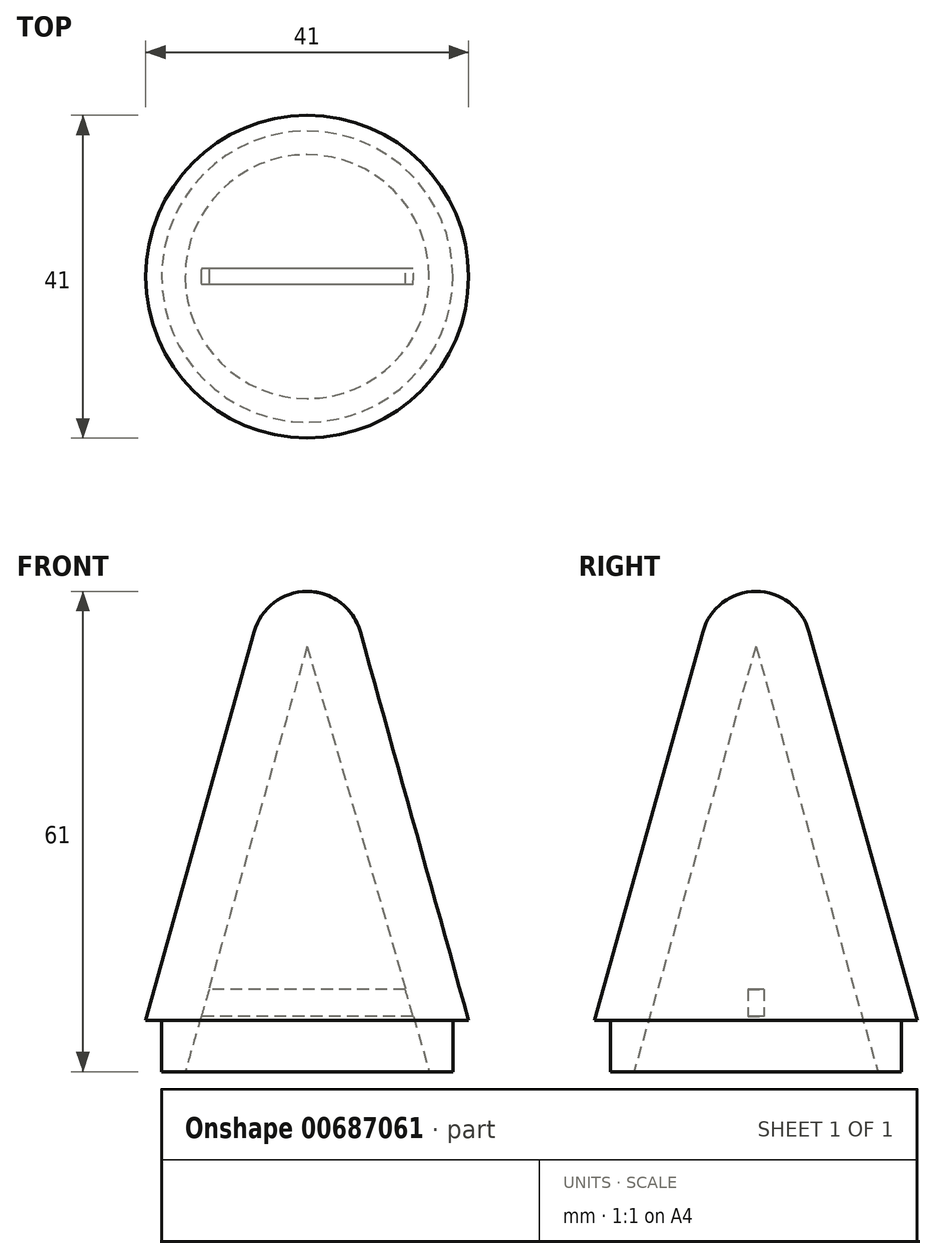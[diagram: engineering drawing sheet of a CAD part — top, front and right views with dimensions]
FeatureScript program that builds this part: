
annotation { "Feature Type Name" : "Feature", "Feature Type Description" : "" }
export const myFeature = defineFeature(function(context is Context, id is Id, definition is map)
    precondition{}
    {
        {
            var Q0;
            Q0=qCreatedBy(makeId("Front.planeOp"),FACE);
            var sketch = newSketch(context, id + "F0", { "sketchPlane" : qUnion([Q0])});
            skArc(sketch, "E0", {"start": v(6.74, 52.38) * mm, "mid": v(4.23, 56.07) * mm, "end": v(0, 57.5) * mm});
            skLineSegment(sketch, "E1", {"start": v(0, 50.5) * mm, "end": v(15.5, -3.5) * mm});
            skLineSegment(sketch, "E2", {"start": v(6.74, 52.38) * mm, "end": v(20.5, 3) * mm});
            skLineSegment(sketch, "E3", {"start": v(20.5, 3) * mm, "end": v(18.5, 3) * mm});
            skLineSegment(sketch, "E4", {"start": v(18.5, 3) * mm, "end": v(18.5, -3.5) * mm});
            skLineSegment(sketch, "E5", {"start": v(18.5, -3.5) * mm, "end": v(15.5, -3.5) * mm});
            skLineSegment(sketch, "E6", {"start": v(0, 57.5) * mm, "end": v(0, 0) * mm});
            skLineSegment(sketch, "E7", {"start": v(0, 50.92) * mm, "end": v(-0.12, 50.92) * mm});
            skLineSegment(sketch, "E8", {"start": v(15.5, -3.5) * mm, "end": v(15.5, -3.5) * mm});
            skLineSegment(sketch, "E9", {"start": v(15.5, -3.5) * mm, "end": v(0, -3.5) * mm});
            skSolve(sketch);
        }
        {
            var Q0;
            Q0 = qSketchRegion(id + "F0", true);
            var Q1;
            Q1=sQuery(id+"F0.wireOp",EDGE,"E6");
            revolve(context, id + "F1", {"surfaceOperationType" : NewSurfaceOperationType.NEW, "entities" : qUnion([Q0]), "axis" : qUnion([Q1]), "revolveType" : RevolveType.FULL});
        }
        {
            var Q0;
            Q0=qCreatedBy(makeId("Right.planeOp"),FACE);
            var sketch = newSketch(context, id + "F2", { "sketchPlane" : qUnion([Q0])});
            skLineSegment(sketch, "E10.bottom", {"start": v(-1.04, 3.54) * mm, "end": v(1.04, 3.54) * mm});
            skLineSegment(sketch, "E10.top", {"start": v(-1.04, 6.97) * mm, "end": v(1.04, 6.97) * mm});
            skLineSegment(sketch, "E10.left", {"start": v(-1.04, 3.54) * mm, "end": v(-1.04, 6.97) * mm});
            skLineSegment(sketch, "E10.right", {"start": v(1.04, 3.54) * mm, "end": v(1.04, 6.97) * mm});
            skPoint(sketch, "E10.middle", {"position": v(0, 5.26) * mm});
            skSolve(sketch);
        }
        {
            var Q0;
            Q0 = qSketchRegion(id + "F2", true);
            var Q1;
            Q1=makeQuery(id+"F1.opRevolve","SWEPT_BODY",BODY,{"disambiguationData":[OSD([sQuery(id+"F0.wireOp",EDGE,"E0"),sQuery(id+"F0.wireOp",EDGE,"E1"),sQuery(id+"F0.wireOp",EDGE,"E2"),sQuery(id+"F0.wireOp",EDGE,"E3"),sQuery(id+"F0.wireOp",EDGE,"E4"),sQuery(id+"F0.wireOp",EDGE,"E5"),sQuery(id+"F0.wireOp",EDGE,"E6")])]});
            var Q2;
            Q2=makeQuery(id+"F1.opRevolve","SWEPT_BODY",BODY,{"disambiguationData":[OSD([sQuery(id+"F0.wireOp",EDGE,"E0"),sQuery(id+"F0.wireOp",EDGE,"E1"),sQuery(id+"F0.wireOp",EDGE,"E2"),sQuery(id+"F0.wireOp",EDGE,"E3"),sQuery(id+"F0.wireOp",EDGE,"E4"),sQuery(id+"F0.wireOp",EDGE,"E5"),sQuery(id+"F0.wireOp",EDGE,"E6")])]});
            extrude(context, id + "F3", {"entities" : qUnion([Q0]), "operationType" : NewBodyOperationType.ADD, "endBound" : BoundingType.UP_TO_BODY, "depth" : 25 * mm, "endBoundEntityBody" : qUnion([Q1]), "offsetDistance" : 25 * mm, "hasSecondDirection" : true, "secondDirectionBound" : SecondDirectionBoundingType.UP_TO_BODY, "secondDirectionOppositeDirection" : true, "secondDirectionDepth" : 25 * mm, "secondDirectionBoundEntityBody" : qUnion([Q2])});
        }
    });
